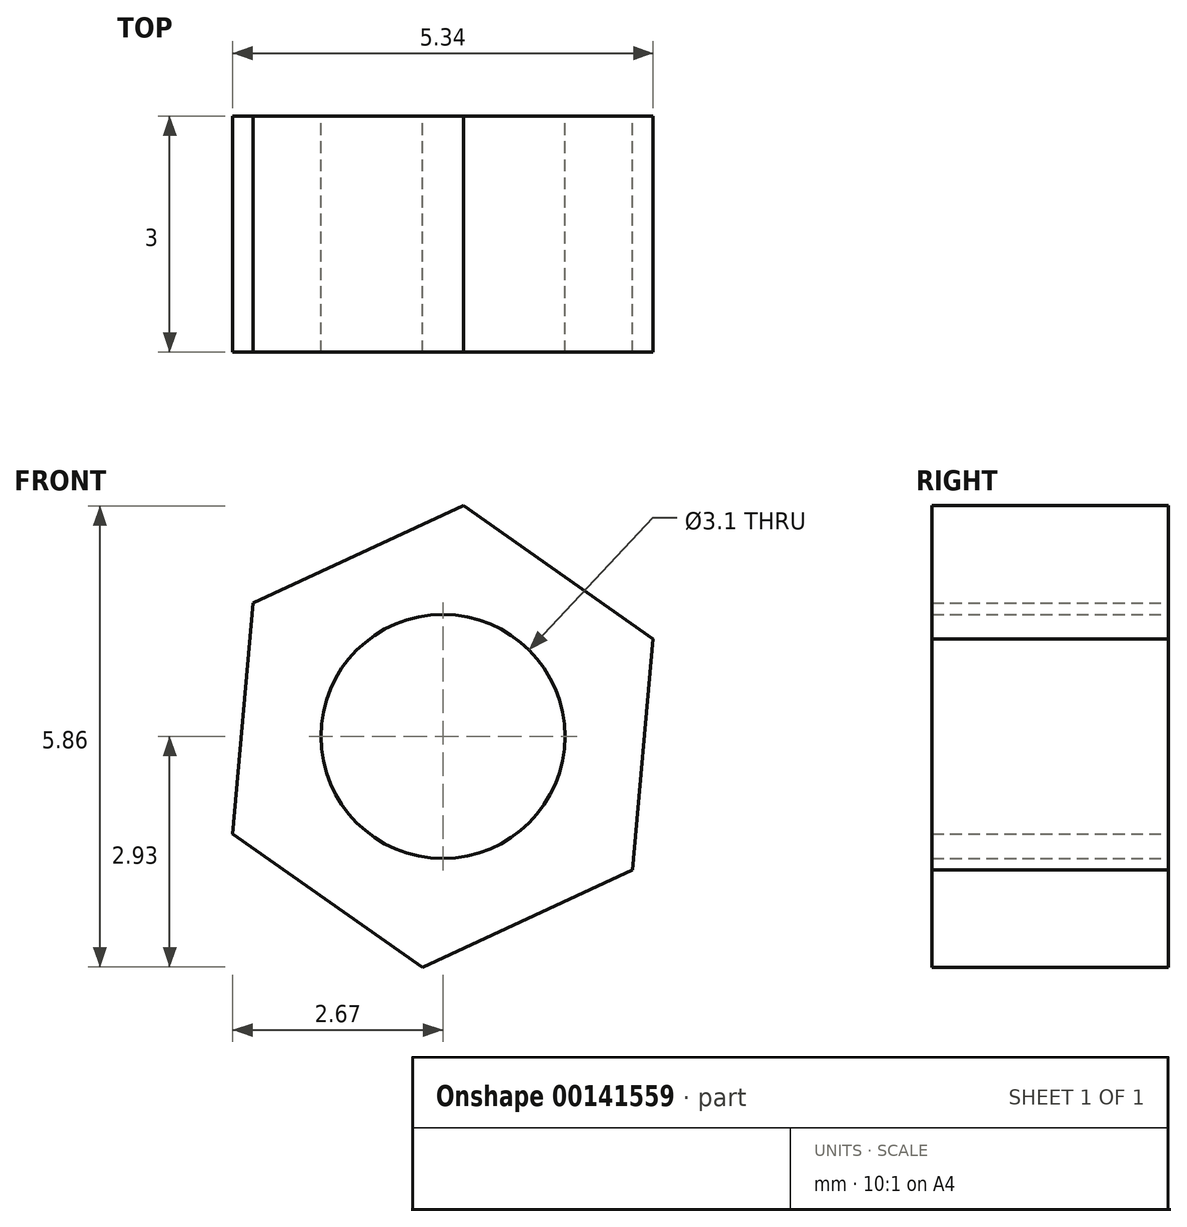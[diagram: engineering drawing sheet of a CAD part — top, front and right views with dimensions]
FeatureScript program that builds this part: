
annotation { "Feature Type Name" : "Feature", "Feature Type Description" : "" }
export const myFeature = defineFeature(function(context is Context, id is Id, definition is map)
    precondition{}
    {
        {
            var Q0;
            Q0=qCreatedBy(makeId("Front.planeOp"),FACE);
            var sketch = newSketch(context, id + "F0", { "sketchPlane" : qUnion([Q0])});
            skCircle(sketch, "E0", {"center": v(0, 0) * mm, "radius": 1.55 * mm});
            skCircle(sketch, "E1.cCircle", {"center": v(0, 0) * mm, "radius": 2.55 * mm, "construction": true});
            skLineSegment(sketch, "E1.0", {"start": v(2.4, -1.7) * mm, "end": v(-0.26, -2.93) * mm});
            skLineSegment(sketch, "E1.1", {"start": v(-0.26, -2.93) * mm, "end": v(-2.67, -1.24) * mm});
            skLineSegment(sketch, "E1.2", {"start": v(-2.67, -1.24) * mm, "end": v(-2.4, 1.7) * mm});
            skLineSegment(sketch, "E1.3", {"start": v(-2.4, 1.7) * mm, "end": v(0.26, 2.93) * mm});
            skLineSegment(sketch, "E1.4", {"start": v(0.26, 2.93) * mm, "end": v(2.67, 1.24) * mm});
            skLineSegment(sketch, "E1.5", {"start": v(2.67, 1.24) * mm, "end": v(2.4, -1.7) * mm});
            skPoint(sketch, "E1.0.midPoint", {"position": v(1.07, -2.31) * mm});
            skSolve(sketch);
        }
        {
            var Q0;
            Q0 = qSketchRegion(id + "F0", true);
            extrude(context, id + "F1", {"entities" : qUnion([Q0]), "depth" : 3 * mm});
        }
    });
